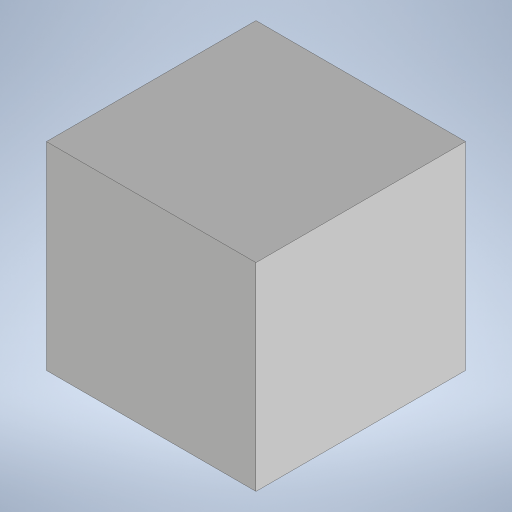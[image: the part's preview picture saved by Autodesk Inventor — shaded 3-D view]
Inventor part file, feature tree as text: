
AUTODESK INVENTOR PART (.ipt)
format: ipt  version: 2024 (Build 280153000, 153)  size: 12,723,712 bytes
history: native  units: mm
features: other x6, plane x1, extrude x1, sketch x1
ambient origin geometry x8: Origin, YZ Plane, XZ Plane, XY Plane, X Axis, Y Axis, Z Axis, Center Point
bodies: Body1 (feature_tree)
feature tree (9):
  other  "M.ipt"
  plane  "Plano de trabajo1"
  extrude  "Extrusión1"  [1 undecoded]
  other  "Combinar1"
  other  "Sólido1::M.ipt"
  other  "OperaciónIdentificador1"
  sketch  "Boceto1"  dims[d0=25.0mm d1=-365.0mm d2=550.0mm d3=520.0mm d4=550.0mm d5=0.0mm]
  other  "Sólido2"
  other  "Sólido1"
note: 1 required parameter value undecoded (feature->parameter linkage not recoverable at this tier; creation-order binding heuristic only, values carry confidence <= 0.55)
